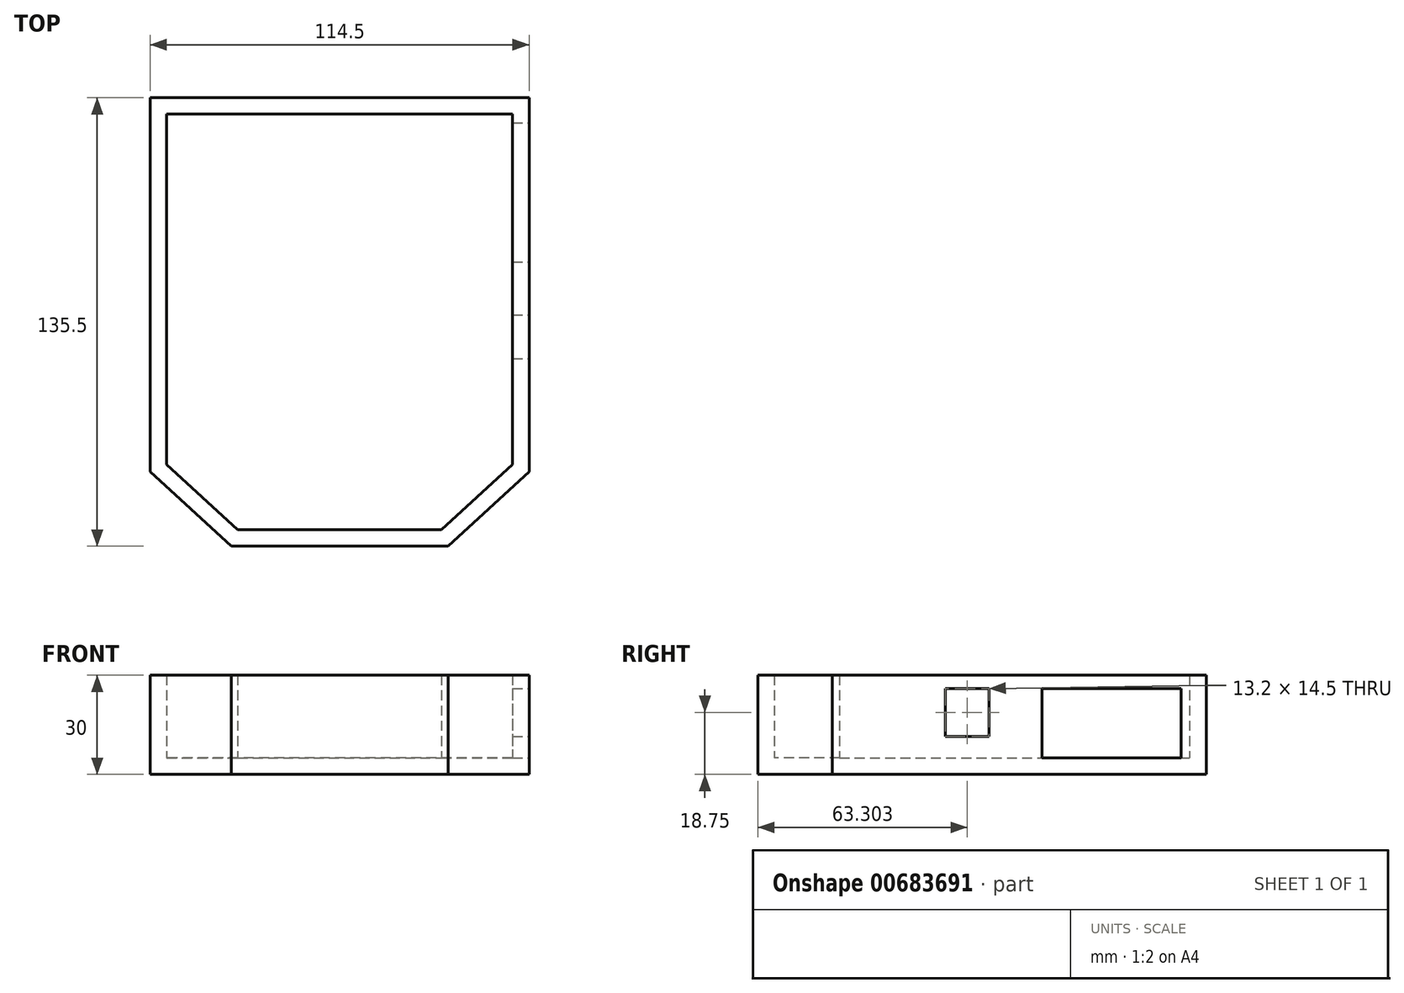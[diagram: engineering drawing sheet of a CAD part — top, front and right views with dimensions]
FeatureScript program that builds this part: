
annotation { "Feature Type Name" : "Feature", "Feature Type Description" : "" }
export const myFeature = defineFeature(function(context is Context, id is Id, definition is map)
    precondition{}
    {
        {
            var Q0;
            Q0=qCreatedBy(makeId("Top.planeOp"),FACE);
            var sketch = newSketch(context, id + "F0", { "sketchPlane" : qUnion([Q0])});
            skLineSegment(sketch, "E0", {"start": v(-46.3, 51.27) * mm, "end": v(68.2, 51.27) * mm});
            skLineSegment(sketch, "E1", {"start": v(68.2, 51.27) * mm, "end": v(68.2, -61.73) * mm});
            skLineSegment(sketch, "E2", {"start": v(43.7, -84.23) * mm, "end": v(-21.8, -84.23) * mm});
            skLineSegment(sketch, "E3", {"start": v(-46.3, -61.73) * mm, "end": v(-46.3, 51.27) * mm});
            skLineSegment(sketch, "E4", {"start": v(-46.3, -61.73) * mm, "end": v(-21.8, -84.23) * mm});
            skLineSegment(sketch, "E5", {"start": v(43.7, -84.23) * mm, "end": v(68.2, -61.73) * mm});
            skSolve(sketch);
        }
        {
            var Q0;
            Q0 = qSketchRegion(id + "F0", true);
            extrude(context, id + "F1", {"entities" : qUnion([Q0]), "depth" : 5 * mm, "offsetDistance" : 25 * mm});
        }
        {
            var Q0;
            Q0=makeQuery(id+"F1.opExtrude","CAP_FACE",FACE,{"disambiguationData":[OSD([sQuery(id+"F0.wireOp",EDGE,"E0"),sQuery(id+"F0.wireOp",EDGE,"E1"),sQuery(id+"F0.wireOp",EDGE,"E2"),sQuery(id+"F0.wireOp",EDGE,"E3"),sQuery(id+"F0.wireOp",EDGE,"E4"),sQuery(id+"F0.wireOp",EDGE,"E5")])],"isStart":false});
            var sketch = newSketch(context, id + "F2", { "sketchPlane" : qUnion([Q0])});
            skLineSegment(sketch, "E6.0", {"start": v(-41.3, -59.53) * mm, "end": v(-19.86, -79.23) * mm});
            skLineSegment(sketch, "E6.1", {"start": v(41.75, -79.23) * mm, "end": v(63.2, -59.53) * mm});
            skLineSegment(sketch, "E6.2", {"start": v(63.2, -59.53) * mm, "end": v(63.2, 46.27) * mm});
            skLineSegment(sketch, "E6.3", {"start": v(-19.86, -79.23) * mm, "end": v(41.75, -79.23) * mm});
            skLineSegment(sketch, "E6.4", {"start": v(63.2, 46.27) * mm, "end": v(-41.3, 46.27) * mm});
            skLineSegment(sketch, "E6.5", {"start": v(-41.3, 46.27) * mm, "end": v(-41.3, -59.53) * mm});
            skSolve(sketch);
        }
        {
            var Q0;
            Q0=makeQuery(id+"F2.imprint","IMPRINT",FACE,{"disambiguationData":[TD([[makeQuery(id+"F2.imprint","IMPRINT",EDGE,{"derivedFrom":sQuery(id+"F2.wireOp",EDGE,"E6.0")}),-1.0]])]});
            extrude(context, id + "F3", {"entities" : qUnion([Q0]), "operationType" : NewBodyOperationType.ADD, "depth" : 25 * mm, "offsetDistance" : 25 * mm});
        }
        {
            var Q0;
            {var subQ0=sQuery(id+"F0.wireOp",EDGE,"E1");Q0=makeQuery(id+"F3.boolean.opBoolean","MERGE",FACE,{"derivedFrom":[makeQuery(id+"F1.opExtrude","SWEPT_FACE",FACE,{"disambiguationData":[OSD([subQ0])]}),makeQuery(id+"F3.opExtrude","SWEPT_FACE",FACE,{"disambiguationData":[OSD([subQ0])]})]});}
            var sketch = newSketch(context, id + "F4", { "sketchPlane" : qUnion([Q0])});
            skSolve(sketch);
        }
        {
            var Q0;
            {var subQ0=sQuery(id+"F0.wireOp",EDGE,"E1");Q0=makeQuery(id+"F4.imprint","IMPRINT",FACE,{"disambiguationData":[TD([[makeQuery(id+"F4.imprint","IMPRINT",EDGE,{"derivedFrom":makeQuery(id+"F1.opExtrude","CAP_EDGE",EDGE,{"disambiguationData":[OSD([subQ0])],"isStart":true})}),-1.0]])]});}
            var sketch = newSketch(context, id + "F5", { "sketchPlane" : qUnion([Q0])});
            skLineSegment(sketch, "E7.bottom", {"start": v(-27.53, 26) * mm, "end": v(-14.33, 26) * mm});
            skLineSegment(sketch, "E7.top", {"start": v(-27.53, 11.5) * mm, "end": v(-14.33, 11.5) * mm});
            skLineSegment(sketch, "E7.left", {"start": v(-27.53, 26) * mm, "end": v(-27.53, 11.5) * mm});
            skLineSegment(sketch, "E7.right", {"start": v(-14.33, 26) * mm, "end": v(-14.33, 11.5) * mm});
            skLineSegment(sketch, "E8.bottom", {"start": v(1.67, 26) * mm, "end": v(43.67, 26) * mm});
            skLineSegment(sketch, "E8.top", {"start": v(1.67, 5) * mm, "end": v(43.67, 5) * mm});
            skLineSegment(sketch, "E8.left", {"start": v(1.67, 26) * mm, "end": v(1.67, 5) * mm});
            skLineSegment(sketch, "E8.right", {"start": v(43.67, 26) * mm, "end": v(43.67, 5) * mm});
            skSolve(sketch);
        }
        {
            var Q0;
            Q0 = qSketchRegion(id + "F5", true);
            extrude(context, id + "F6", {"entities" : qUnion([Q0]), "operationType" : NewBodyOperationType.REMOVE, "endBound" : BoundingType.UP_TO_NEXT, "oppositeDirection" : true, "depth" : 25 * mm, "offsetDistance" : 25 * mm});
        }
    });
